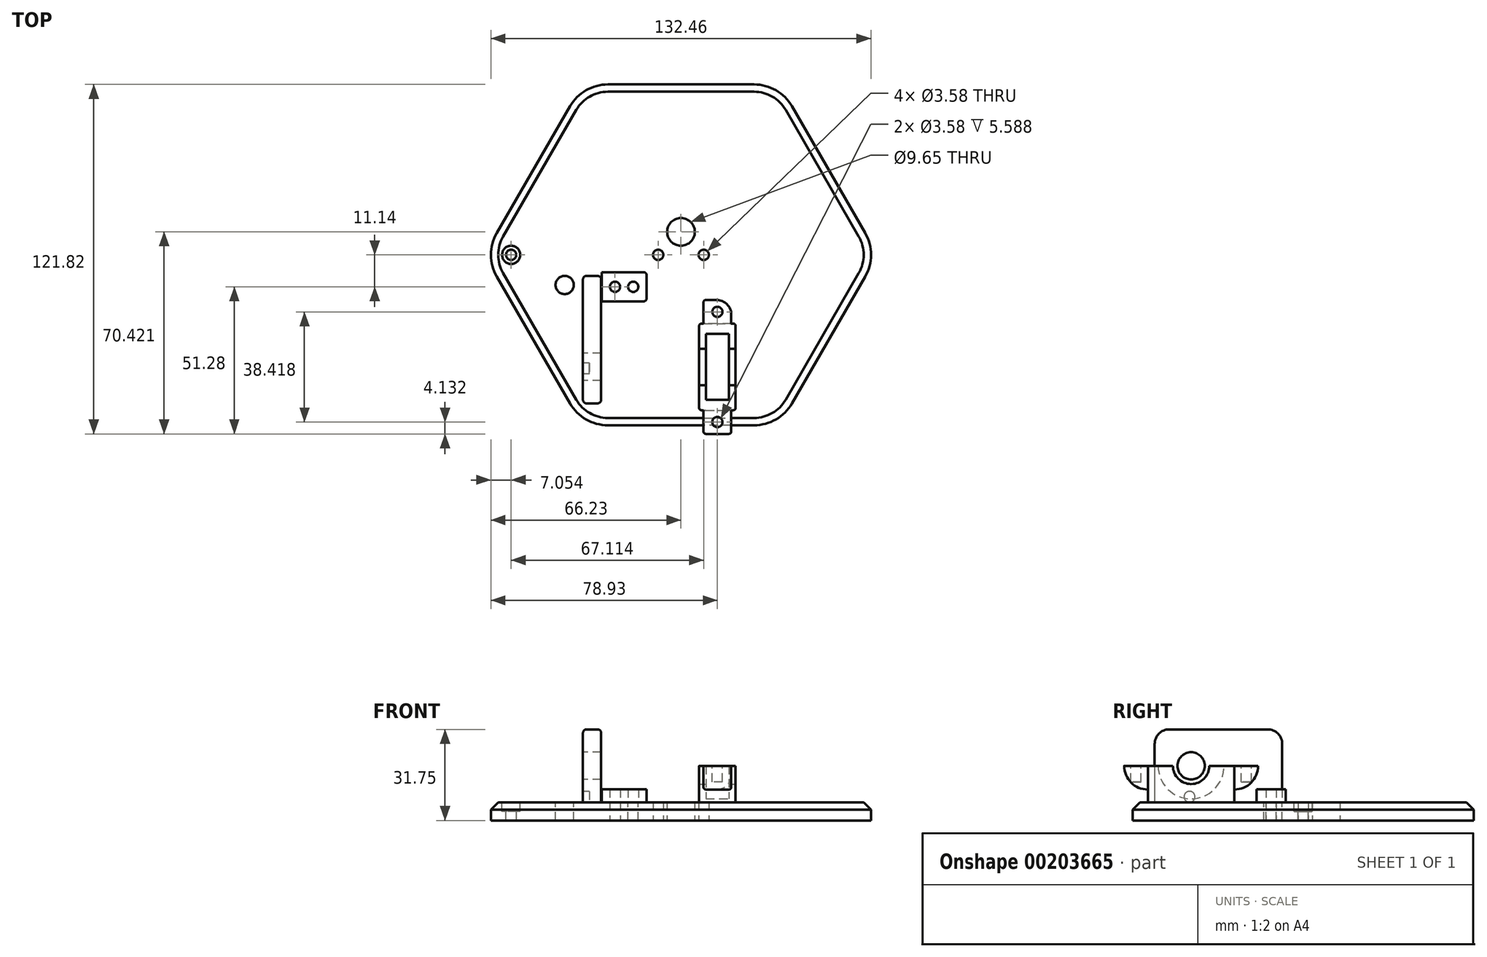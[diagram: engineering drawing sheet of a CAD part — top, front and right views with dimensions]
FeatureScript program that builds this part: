
annotation { "Feature Type Name" : "Feature", "Feature Type Description" : "" }
export const myFeature = defineFeature(function(context is Context, id is Id, definition is map)
    precondition{}
    {
        {
            var Q0;
            Q0=qCreatedBy(makeId("Top.planeOp"),FACE);
            var sketch = newSketch(context, id + "F0", { "sketchPlane" : qUnion([Q0])});
            skCircle(sketch, "E0.cCircle", {"center": v(0, 0) * mm, "radius": 59.4 * mm, "construction": true});
            skLineSegment(sketch, "E0.0", {"start": v(34.3, -59.4) * mm, "end": v(-34.3, -59.4) * mm});
            skLineSegment(sketch, "E0.1", {"start": v(-34.3, -59.4) * mm, "end": v(-68.59, 0) * mm});
            skLineSegment(sketch, "E0.2", {"start": v(-68.59, 0) * mm, "end": v(-34.3, 59.4) * mm});
            skLineSegment(sketch, "E0.3", {"start": v(-34.3, 59.4) * mm, "end": v(34.3, 59.4) * mm});
            skLineSegment(sketch, "E0.4", {"start": v(34.3, 59.4) * mm, "end": v(68.59, 0) * mm});
            skLineSegment(sketch, "E0.5", {"start": v(68.59, 0) * mm, "end": v(34.3, -59.4) * mm});
            skPoint(sketch, "E0.0.midPoint", {"position": v(0, -59.4) * mm});
            skCircle(sketch, "E1", {"center": v(0, 0) * mm, "radius": 3.18 * mm});
            skCircle(sketch, "E2", {"center": v(0, 8) * mm, "radius": 4.83 * mm});
            skCircle(sketch, "E3", {"center": v(0, 0) * mm, "radius": 7.94 * mm, "construction": true});
            skCircle(sketch, "E4", {"center": v(-7.94, 0) * mm, "radius": 1.8 * mm});
            skCircle(sketch, "E5", {"center": v(7.94, 0) * mm, "radius": 1.8 * mm});
            skSolve(sketch);
        }
        {
            var Q0;
            Q0=makeQuery(id+"F0.imprint","IMPRINT",FACE,{"disambiguationData":[TD([[makeQuery(id+"F0.imprint","IMPRINT",EDGE,{"derivedFrom":sQuery(id+"F0.wireOp",EDGE,"E0.0")}),-1.0]])]});
            var Q1;
            Q1=makeQuery(id+"F0.imprint","IMPRINT",FACE,{"disambiguationData":[TD([[makeQuery(id+"F0.imprint","IMPRINT",EDGE,{"derivedFrom":sQuery(id+"F0.wireOp",EDGE,"E1")}),1.0]])]});
            extrude(context, id + "F1", {"entities" : qUnion([Q0, Q1]), "depth" : 6.35 * mm});
        }
        {
            var Q0;
            Q0=makeQuery(id+"F1.opExtrude","CAP_FACE",FACE,{"disambiguationData":[OSD([sQuery(id+"F0.wireOp",EDGE,"E0.0"),sQuery(id+"F0.wireOp",EDGE,"E0.1"),sQuery(id+"F0.wireOp",EDGE,"E0.2"),sQuery(id+"F0.wireOp",EDGE,"E0.3"),sQuery(id+"F0.wireOp",EDGE,"E0.4"),sQuery(id+"F0.wireOp",EDGE,"E0.5"),sQuery(id+"F0.wireOp",EDGE,"E1")])],"isStart":false});
            var sketch = newSketch(context, id + "F2", { "sketchPlane" : qUnion([Q0])});
            skLineSegment(sketch, "E6.bottom", {"start": v(-34.16, -51.78) * mm, "end": v(-27.81, -51.78) * mm});
            skLineSegment(sketch, "E6.top", {"start": v(-34.16, -7.33) * mm, "end": v(-27.81, -7.33) * mm});
            skLineSegment(sketch, "E6.left", {"start": v(-34.16, -51.78) * mm, "end": v(-34.16, -7.33) * mm});
            skLineSegment(sketch, "E6.right", {"start": v(-27.81, -51.78) * mm, "end": v(-27.81, -7.33) * mm});
            skLineSegment(sketch, "E7.bottom", {"start": v(6.35, -54.16) * mm, "end": v(19.05, -54.16) * mm});
            skLineSegment(sketch, "E7.top", {"start": v(6.35, -24) * mm, "end": v(19.05, -24) * mm});
            skLineSegment(sketch, "E7.left", {"start": v(6.35, -54.16) * mm, "end": v(6.35, -24) * mm});
            skLineSegment(sketch, "E7.right", {"start": v(19.05, -54.16) * mm, "end": v(19.05, -24) * mm});
            skLineSegment(sketch, "E8.1.0", {"start": v(37.38, 43.58) * mm, "end": v(11.26, 28.5) * mm});
            skLineSegment(sketch, "E8.1.1", {"start": v(43.73, 32.58) * mm, "end": v(17.6, 17.5) * mm});
            skLineSegment(sketch, "E8.1.2", {"start": v(17.6, 17.5) * mm, "end": v(11.26, 28.5) * mm});
            skLineSegment(sketch, "E8.1.3", {"start": v(61.92, -3.7) * mm, "end": v(23.43, -25.92) * mm});
            skLineSegment(sketch, "E8.1.4", {"start": v(58.75, 1.8) * mm, "end": v(20.25, -20.42) * mm});
            skLineSegment(sketch, "E8.1.5", {"start": v(20.25, -20.42) * mm, "end": v(14.92, -11.18) * mm});
            skLineSegment(sketch, "E8.1.6", {"start": v(26.85, -16.61) * mm, "end": v(21.52, -7.37) * mm});
            skLineSegment(sketch, "E8.1.7", {"start": v(43.73, 32.58) * mm, "end": v(37.38, 43.58) * mm});
            skLineSegment(sketch, "E8.1.8", {"start": v(14.92, -11.18) * mm, "end": v(21.52, -7.37) * mm});
            skLineSegment(sketch, "E8.1.9", {"start": v(61.92, -3.7) * mm, "end": v(58.75, 1.8) * mm});
            skLineSegment(sketch, "E8.1.10", {"start": v(23.43, -25.92) * mm, "end": v(20.25, -20.42) * mm});
            skLineSegment(sketch, "E8.1.11", {"start": v(20.25, -20.42) * mm, "end": v(26.85, -16.61) * mm});
            skLineSegment(sketch, "E8.2.0", {"start": v(-56.43, 10.58) * mm, "end": v(-30.3, -4.5) * mm});
            skLineSegment(sketch, "E8.2.1", {"start": v(-50.08, 21.58) * mm, "end": v(-23.96, 6.5) * mm});
            skLineSegment(sketch, "E8.2.2", {"start": v(-23.96, 6.5) * mm, "end": v(-30.3, -4.5) * mm});
            skLineSegment(sketch, "E8.2.3", {"start": v(-27.76, 55.47) * mm, "end": v(10.74, 33.25) * mm});
            skLineSegment(sketch, "E8.2.4", {"start": v(-30.93, 49.98) * mm, "end": v(7.56, 27.75) * mm});
            skLineSegment(sketch, "E8.2.5", {"start": v(7.56, 27.75) * mm, "end": v(2.23, 18.51) * mm});
            skLineSegment(sketch, "E8.2.6", {"start": v(0.96, 31.56) * mm, "end": v(-4.37, 22.32) * mm});
            skLineSegment(sketch, "E8.2.7", {"start": v(-50.08, 21.58) * mm, "end": v(-56.43, 10.58) * mm});
            skLineSegment(sketch, "E8.2.8", {"start": v(2.23, 18.51) * mm, "end": v(-4.37, 22.32) * mm});
            skLineSegment(sketch, "E8.2.9", {"start": v(-27.76, 55.47) * mm, "end": v(-30.93, 49.98) * mm});
            skLineSegment(sketch, "E8.2.10", {"start": v(10.74, 33.25) * mm, "end": v(7.56, 27.75) * mm});
            skLineSegment(sketch, "E8.2.11", {"start": v(7.56, 27.75) * mm, "end": v(0.96, 31.56) * mm});
            skPoint(sketch, "E8.center", {"position": v(0, 0) * mm});
            skCircle(sketch, "E9", {"center": v(-40.51, -10.5) * mm, "radius": 3.18 * mm});
            skCircle(sketch, "E10", {"center": v(-59.18, 0) * mm, "radius": 1.8 * mm});
            skCircle(sketch, "E11", {"center": v(-59.18, 0) * mm, "radius": 3.18 * mm});
            skCircle(sketch, "E12.1.0", {"center": v(29.59, -51.25) * mm, "radius": 3.18 * mm});
            skCircle(sketch, "E12.1.1", {"center": v(29.59, -51.25) * mm, "radius": 1.8 * mm});
            skCircle(sketch, "E12.2.0", {"center": v(29.59, 51.25) * mm, "radius": 3.18 * mm});
            skCircle(sketch, "E12.2.1", {"center": v(29.59, 51.25) * mm, "radius": 1.8 * mm});
            skCircle(sketch, "E13", {"center": v(-22.97, -11.14) * mm, "radius": 1.8 * mm});
            skPoint(sketch, "E13.centerSnap0", {"position": v(-16.64, -11.14) * mm});
            skCircle(sketch, "E14", {"center": v(-16.62, -11.14) * mm, "radius": 1.8 * mm});
            skCircle(sketch, "E15", {"center": v(0, 0) * mm, "radius": 4.76 * mm});
            skLineSegment(sketch, "E16", {"start": v(-22.97, -11.14) * mm, "end": v(-16.62, -11.14) * mm, "construction": true});
            skLineSegment(sketch, "E17.bottom", {"start": v(-11.98, -6.06) * mm, "end": v(-27.62, -6.06) * mm});
            skLineSegment(sketch, "E17.top", {"start": v(-11.98, -16.22) * mm, "end": v(-27.62, -16.22) * mm});
            skLineSegment(sketch, "E17.left", {"start": v(-11.98, -6.06) * mm, "end": v(-11.98, -16.22) * mm});
            skLineSegment(sketch, "E17.right", {"start": v(-27.62, -6.06) * mm, "end": v(-27.62, -16.22) * mm});
            skPoint(sketch, "E17.middle", {"position": v(-19.8, -11.14) * mm});
            skSolve(sketch);
        }
        {
            var Q0;
            Q0=makeQuery(id+"F2.imprint","IMPRINT",FACE,{"disambiguationData":[TD([[makeQuery(id+"F2.imprint","IMPRINT",EDGE,{"derivedFrom":sQuery(id+"F2.wireOp",EDGE,"E6.bottom")}),1.0]])]});
            extrude(context, id + "F3", {"entities" : qUnion([Q0]), "operationType" : NewBodyOperationType.ADD, "depth" : 25.4 * mm});
        }
        {
            var Q0;
            Q0=makeQuery(id+"F2.imprint","IMPRINT",FACE,{"disambiguationData":[TD([[makeQuery(id+"F2.imprint","IMPRINT",EDGE,{"derivedFrom":sQuery(id+"F2.wireOp",EDGE,"E7.bottom")}),1.0]])]});
            extrude(context, id + "F4", {"entities" : qUnion([Q0]), "operationType" : NewBodyOperationType.ADD, "depth" : 12.7 * mm});
        }
        {
            var Q0;
            Q0=makeQuery(id+"F2.imprint","IMPRINT",FACE,{"disambiguationData":[TD([[makeQuery(id+"F2.imprint","IMPRINT",EDGE,{"derivedFrom":sQuery(id+"F2.wireOp",EDGE,"E9")}),1.0]])]});
            extrude(context, id + "F5", {"entities" : qUnion([Q0]), "operationType" : NewBodyOperationType.REMOVE, "oppositeDirection" : true, "depth" : 25.4 * mm});
        }
        {
            var Q0;
            Q0=sQuery(id+"F2.wireOp",VERTEX,"E10.center");
            var Q1;
            Q1=makeQuery(id+"F1.opExtrude","SWEPT_BODY",BODY,{"disambiguationData":[OSD([sQuery(id+"F0.wireOp",EDGE,"E0.0"),sQuery(id+"F0.wireOp",EDGE,"E0.1"),sQuery(id+"F0.wireOp",EDGE,"E0.2"),sQuery(id+"F0.wireOp",EDGE,"E0.3"),sQuery(id+"F0.wireOp",EDGE,"E0.4"),sQuery(id+"F0.wireOp",EDGE,"E0.5"),sQuery(id+"F0.wireOp",EDGE,"E1")])]});
            hole(context, id + "F6", {"style" : HoleStyle.C_BORE, "endStyle" : HoleEndStyle.BLIND, "holeDiameter" : 3.58 * mm, "cBoreDiameter" : 6.35 * mm, "cBoreDepth" : 3.17 * mm, "holeDepth" : 6.35 * mm, "locations" : qUnion([Q0]), "scope" : qUnion([Q1])});
        }
        {
            var Q0;
            Q0=makeQuery(id+"F2.imprint","IMPRINT",FACE,{"disambiguationData":[TD([[makeQuery(id+"F2.imprint","IMPRINT",EDGE,{"derivedFrom":sQuery(id+"F2.wireOp",EDGE,"E13")}),-1.0]])]});
            extrude(context, id + "F7", {"entities" : qUnion([Q0]), "operationType" : NewBodyOperationType.ADD, "depth" : 4.57 * mm});
        }
        {
            var Q0;
            Q0=makeQuery(id+"F7.opExtrude","SWEPT_EDGE",EDGE,{"disambiguationData":[OSD([sQuery(id+"F2.wireOp",EDGE,"E17.top"),sQuery(id+"F2.wireOp",EDGE,"E17.left")])]});
            var Q1;
            Q1=makeQuery(id+"F7.opExtrude","SWEPT_EDGE",EDGE,{"disambiguationData":[OSD([sQuery(id+"F2.wireOp",EDGE,"E17.bottom"),sQuery(id+"F2.wireOp",EDGE,"E17.left")])]});
            fillet(context, id + "F8", {"entities" : qUnion([Q0, Q1]), "radius" : 1.02 * mm, "tangentPropagation" : true, "allowEdgeOverflow" : false});
        }
        {
            var Q0;
            Q0=makeQuery(id+"F4.opExtrude","CAP_FACE",FACE,{"disambiguationData":[OSD([sQuery(id+"F2.wireOp",EDGE,"E7.bottom"),sQuery(id+"F2.wireOp",EDGE,"E7.top"),sQuery(id+"F2.wireOp",EDGE,"E7.left"),sQuery(id+"F2.wireOp",EDGE,"E7.right")])],"isStart":false});
            var sketch = newSketch(context, id + "F9", { "sketchPlane" : qUnion([Q0])});
            skLineSegment(sketch, "E18.bottom", {"start": v(16.7, -27.58) * mm, "end": v(8.7, -27.58) * mm});
            skLineSegment(sketch, "E18.top", {"start": v(16.7, -50.58) * mm, "end": v(8.7, -50.58) * mm});
            skLineSegment(sketch, "E18.left", {"start": v(16.7, -27.58) * mm, "end": v(16.7, -50.58) * mm});
            skLineSegment(sketch, "E18.right", {"start": v(8.7, -27.58) * mm, "end": v(8.7, -50.58) * mm});
            skPoint(sketch, "E18.middle", {"position": v(12.7, -39.08) * mm});
            skPoint(sketch, "E18.middle.positionSnap0", {"position": v(12.7, -24) * mm});
            skPoint(sketch, "E18.middle.positionSnap1", {"position": v(6.35, -39.08) * mm});
            skPoint(sketch, "E18.centerSnap0", {"position": v(12.7, -24) * mm});
            skPoint(sketch, "E18.centerSnap1", {"position": v(6.35, -39.08) * mm});
            skLineSegment(sketch, "E19", {"start": v(8.7, -39.08) * mm, "end": v(16.7, -39.08) * mm});
            skSolve(sketch);
        }
        {
            var Q0;
            Q0=makeQuery(id+"F9.imprint","IMPRINT",FACE,{"disambiguationData":[TD([[makeQuery(id+"F9.imprint","IMPRINT",EDGE,{"derivedFrom":sQuery(id+"F9.wireOp",EDGE,"E18.bottom")}),1.0]])]});
            var Q1;
            Q1=sQuery(id+"F9.wireOp",EDGE,"E19");
            revolve(context, id + "F10", {"operationType" : NewBodyOperationType.REMOVE, "entities" : qUnion([Q0]), "axis" : qUnion([Q1]), "revolveType" : RevolveType.FULL, "oppositeDirection" : true});
        }
        {
            var Q0;
            Q0=makeQuery(id+"F4.opExtrude","SWEPT_FACE",FACE,{"disambiguationData":[OSD([sQuery(id+"F2.wireOp",EDGE,"E7.top")])]});
            var sketch = newSketch(context, id + "F11", { "sketchPlane" : qUnion([Q0])});
            skLineSegment(sketch, "E20", {"start": v(-12.7, 19.05) * mm, "end": v(-12.7, 10.8) * mm});
            skLineSegment(sketch, "E21.bottom", {"start": v(-17.53, 19.05) * mm, "end": v(-7.87, 19.05) * mm});
            skLineSegment(sketch, "E21.top", {"start": v(-17.53, 10.8) * mm, "end": v(-7.87, 10.8) * mm});
            skLineSegment(sketch, "E21.left", {"start": v(-17.53, 19.05) * mm, "end": v(-17.53, 10.8) * mm});
            skLineSegment(sketch, "E21.right", {"start": v(-7.87, 19.05) * mm, "end": v(-7.87, 10.8) * mm});
            skPoint(sketch, "E21.middle", {"position": v(-12.7, 14.92) * mm});
            skSolve(sketch);
        }
        {
            var Q0;
            Q0=makeQuery(id+"F4.opExtrude","SWEPT_FACE",FACE,{"disambiguationData":[OSD([sQuery(id+"F2.wireOp",EDGE,"E7.bottom")])]});
            var sketch = newSketch(context, id + "F12", { "sketchPlane" : qUnion([Q0])});
            skLineSegment(sketch, "E22", {"start": v(12.7, 19.05) * mm, "end": v(12.7, 10.8) * mm});
            skPoint(sketch, "E22.endSnap0", {"position": v(12.7, 19.05) * mm});
            skLineSegment(sketch, "E23.bottom", {"start": v(7.87, 19.05) * mm, "end": v(17.53, 19.05) * mm});
            skLineSegment(sketch, "E23.top", {"start": v(7.87, 10.8) * mm, "end": v(17.53, 10.8) * mm});
            skLineSegment(sketch, "E23.left", {"start": v(7.87, 19.05) * mm, "end": v(7.87, 10.8) * mm});
            skLineSegment(sketch, "E23.right", {"start": v(17.53, 19.05) * mm, "end": v(17.53, 10.8) * mm});
            skPoint(sketch, "E23.middle", {"position": v(12.7, 14.92) * mm});
            skSolve(sketch);
        }
        {
            var Q0;
            Q0=sQuery(id+"F2.wireOp",VERTEX,"E13.center");
            var Q1;
            Q1=sQuery(id+"F2.wireOp",VERTEX,"E13.centerSnap0");
            var Q2;
            Q2=makeQuery(id+"F1.opExtrude","SWEPT_BODY",BODY,{"disambiguationData":[OSD([sQuery(id+"F0.wireOp",EDGE,"E0.0"),sQuery(id+"F0.wireOp",EDGE,"E0.1"),sQuery(id+"F0.wireOp",EDGE,"E0.2"),sQuery(id+"F0.wireOp",EDGE,"E0.3"),sQuery(id+"F0.wireOp",EDGE,"E0.4"),sQuery(id+"F0.wireOp",EDGE,"E0.5"),sQuery(id+"F0.wireOp",EDGE,"E1")])]});
            hole(context, id + "F13", {"style" : HoleStyle.SIMPLE, "endStyle" : HoleEndStyle.BLIND, "holeDiameter" : 3.58 * mm, "holeDepth" : 6.35 * mm, "locations" : qUnion([Q0, Q1]), "scope" : qUnion([Q2])});
        }
        {
            var Q0;
            {var subQ0=sQuery(id+"F11.wireOp",EDGE,"E20");Q0=makeQuery(id+"F11.imprint","IMPRINT",FACE,{"disambiguationData":[TD([[makeQuery(id+"F11.imprint","IMPRINT",EDGE,{"derivedFrom":subQ0}),-1.0]])]});}
            var Q1;
            {var subQ0=sQuery(id+"F11.wireOp",EDGE,"E20");Q1=makeQuery(id+"F11.imprint","IMPRINT",FACE,{"disambiguationData":[TD([[makeQuery(id+"F11.imprint","IMPRINT",EDGE,{"derivedFrom":subQ0}),1.0]])]});}
            var Q2;
            Q2=sQuery(id+"F11.wireOp",EDGE,"E21.bottom");
            revolve(context, id + "F14", {"operationType" : NewBodyOperationType.ADD, "entities" : qUnion([Q0, Q1]), "axis" : qUnion([Q2]), "revolveType" : RevolveType.ONE_DIRECTION, "oppositeDirection" : true, "angle" : 90 * degree});
        }
        {
            var Q0;
            {var subQ0=sQuery(id+"F12.wireOp",EDGE,"E22");Q0=makeQuery(id+"F12.imprint","IMPRINT",FACE,{"disambiguationData":[TD([[makeQuery(id+"F12.imprint","IMPRINT",EDGE,{"derivedFrom":subQ0}),-1.0]])]});}
            var Q1;
            {var subQ0=sQuery(id+"F12.wireOp",EDGE,"E22");Q1=makeQuery(id+"F12.imprint","IMPRINT",FACE,{"disambiguationData":[TD([[makeQuery(id+"F12.imprint","IMPRINT",EDGE,{"derivedFrom":subQ0}),1.0]])]});}
            var Q2;
            Q2=sQuery(id+"F12.wireOp",EDGE,"E23.bottom");
            revolve(context, id + "F15", {"operationType" : NewBodyOperationType.ADD, "entities" : qUnion([Q0, Q1]), "axis" : qUnion([Q2]), "revolveType" : RevolveType.ONE_DIRECTION, "oppositeDirection" : true, "angle" : 90 * degree});
        }
        {
            var Q0;
            Q0=makeQuery(id+"F4.opExtrude","SWEPT_FACE",FACE,{"disambiguationData":[OSD([sQuery(id+"F2.wireOp",EDGE,"E7.right")])]});
            var sketch = newSketch(context, id + "F16", { "sketchPlane" : qUnion([Q0])});
            skCircle(sketch, "E24", {"center": v(-39.08, 19.05) * mm, "radius": 6.35 * mm});
            skSolve(sketch);
        }
        {
            var Q0;
            {var subQ0=sQuery(id+"F16.wireOp",EDGE,"E24");var subQ1=makeQuery(id+"F4.opExtrude","CAP_EDGE",EDGE,{"disambiguationData":[OSD([sQuery(id+"F2.wireOp",EDGE,"E7.right")])],"isStart":false});var subQ2=makeQuery(id+"F16.imprint","INTERSECT",VERTEX,{"disambiguationData":[OD(0.0)],"derivedFrom":[subQ1,subQ0]});Q0=makeQuery(id+"F16.imprint","IMPRINT",FACE,{"disambiguationData":[TD([[makeQuery(id+"F16.imprint","IMPRINT",EDGE,{"disambiguationData":[TD([[subQ2,1.0]])],"derivedFrom":subQ0}),1.0]])]});}
            var Q1;
            {var subQ0=sQuery(id+"F16.wireOp",EDGE,"E24");var subQ1=makeQuery(id+"F4.opExtrude","CAP_EDGE",EDGE,{"disambiguationData":[OSD([sQuery(id+"F2.wireOp",EDGE,"E7.right")])],"isStart":false});var subQ2=makeQuery(id+"F16.imprint","INTERSECT",VERTEX,{"disambiguationData":[OD(0.0)],"derivedFrom":[subQ1,subQ0]});Q1=makeQuery(id+"F16.imprint","IMPRINT",FACE,{"disambiguationData":[TD([[makeQuery(id+"F16.imprint","IMPRINT",EDGE,{"disambiguationData":[TD([[subQ2,-1.0]])],"derivedFrom":subQ0}),1.0]])]});}
            extrude(context, id + "F17", {"entities" : qUnion([Q0, Q1]), "operationType" : NewBodyOperationType.REMOVE, "oppositeDirection" : true, "depth" : 25.4 * mm});
        }
        {
            var Q0;
            Q0=makeQuery(id+"F3.opExtrude","SWEPT_FACE",FACE,{"disambiguationData":[OSD([sQuery(id+"F2.wireOp",EDGE,"E6.left")])]});
            var sketch = newSketch(context, id + "F18", { "sketchPlane" : qUnion([Q0])});
            skCircle(sketch, "E25", {"center": v(39.08, 19.05) * mm, "radius": 4.76 * mm});
            skSolve(sketch);
        }
        {
            var Q0;
            Q0 = qSketchRegion(id + "F18", true);
            extrude(context, id + "F19", {"entities" : qUnion([Q0]), "operationType" : NewBodyOperationType.REMOVE, "oppositeDirection" : true, "depth" : 19.05 * mm});
        }
        {
            var Q0;
            Q0=makeQuery(id+"F3.opExtrude","SWEPT_FACE",FACE,{"disambiguationData":[OSD([sQuery(id+"F2.wireOp",EDGE,"E6.left")])]});
            var sketch = newSketch(context, id + "F20", { "sketchPlane" : qUnion([Q0])});
            skCircle(sketch, "E26", {"center": v(39.64, 8.26) * mm, "radius": 1.9 * mm});
            skSolve(sketch);
        }
        {
            var Q0;
            {var subQ0=sQuery(id+"F20.wireOp",EDGE,"E26");var subQ1=sQuery(id+"F2.wireOp",EDGE,"E6.left");var subQ2=makeQuery(id+"F26.opFillet","BLEND_EDGE",EDGE,{"blendedFrom":[makeQuery(id+"F3.opExtrude","CAP_EDGE",EDGE,{"disambiguationData":[OSD([subQ1])],"isStart":true}),makeQuery(id+"F3.opExtrude","SWEPT_FACE",FACE,{"disambiguationData":[OSD([subQ1])]})],"blendedInto":[makeQuery(id+"F3.opExtrude","SWEPT_FACE",FACE,{"disambiguationData":[OSD([subQ1])]})]});var subQ3=makeQuery(id+"F20.imprint","INTERSECT",VERTEX,{"disambiguationData":[OD(0.0)],"derivedFrom":[subQ2,subQ0]});Q0=makeQuery(id+"F20.imprint","IMPRINT",FACE,{"disambiguationData":[TD([[makeQuery(id+"F20.imprint","IMPRINT",EDGE,{"disambiguationData":[TD([[subQ3,1.0]])],"derivedFrom":subQ0}),1.0]])]});}
            var Q1;
            {var subQ0=sQuery(id+"F20.wireOp",EDGE,"E26");var subQ1=sQuery(id+"F2.wireOp",EDGE,"E6.left");var subQ2=makeQuery(id+"F26.opFillet","BLEND_EDGE",EDGE,{"blendedFrom":[makeQuery(id+"F3.opExtrude","CAP_EDGE",EDGE,{"disambiguationData":[OSD([subQ1])],"isStart":true}),makeQuery(id+"F3.opExtrude","SWEPT_FACE",FACE,{"disambiguationData":[OSD([subQ1])]})],"blendedInto":[makeQuery(id+"F3.opExtrude","SWEPT_FACE",FACE,{"disambiguationData":[OSD([subQ1])]})]});var subQ3=makeQuery(id+"F20.imprint","INTERSECT",VERTEX,{"disambiguationData":[OD(0.0)],"derivedFrom":[subQ2,subQ0]});Q1=makeQuery(id+"F20.imprint","IMPRINT",FACE,{"disambiguationData":[TD([[makeQuery(id+"F20.imprint","IMPRINT",EDGE,{"disambiguationData":[TD([[subQ3,-1.0]])],"derivedFrom":subQ0}),1.0]])]});}
            extrude(context, id + "F21", {"entities" : qUnion([Q0, Q1]), "operationType" : NewBodyOperationType.REMOVE, "endBound" : BoundingType.SYMMETRIC, "oppositeDirection" : true, "depth" : 4.57 * mm});
        }
        {
            var Q0;
            {var subQ0=sQuery(id+"F11.wireOp",EDGE,"E21.right");var subQ1=sQuery(id+"F2.wireOp",EDGE,"E7.right");var subQ2=sQuery(id+"F2.wireOp",EDGE,"E7.left");var subQ3=sQuery(id+"F2.wireOp",EDGE,"E7.top");var subQ4=sQuery(id+"F11.wireOp",EDGE,"E21.top");var subQ5=sQuery(id+"F11.wireOp",EDGE,"E21.left");var subQ6=sQuery(id+"F2.wireOp",EDGE,"E7.bottom");Q0=makeQuery(id+"F17.boolean.opBoolean","SPLIT",FACE,{"disambiguationData":[TD([makeQuery(id+"F4.opExtrude","SWEPT_FACE",FACE,{"disambiguationData":[OSD([subQ3])]})])],"derivedFrom":makeQuery(id+"FIzczD0P8AIGJL4_1.boolean.opBoolean","MERGE",FACE,{"derivedFrom":[makeQuery(id+"F14.boolean.opBoolean","MERGE",FACE,{"derivedFrom":[makeQuery(id+"F4.opExtrude","CAP_FACE",FACE,{"disambiguationData":[OSD([subQ6,subQ3,subQ2,subQ1])],"isStart":false}),makeQuery(id+"F14.opRevolve","CAP_FACE",FACE,{"disambiguationData":[OSD([sQuery(id+"F11.wireOp",EDGE,"E21.bottom"),subQ4,subQ5,subQ0])],"isStart":false})]}),makeQuery(id+"FIzczD0P8AIGJL4_1.opRevolve","CAP_FACE",FACE,{"disambiguationData":[OSD([subQ6,sQuery(id+"F12.wireOp",EDGE,"E23.top"),sQuery(id+"F12.wireOp",EDGE,"E23.left"),sQuery(id+"F12.wireOp",EDGE,"E23.right")])],"isStart":false})]})});}
            var sketch = newSketch(context, id + "F22", { "sketchPlane" : qUnion([Q0])});
            skCircle(sketch, "E27", {"center": v(12.7, -19.87) * mm, "radius": 1.8 * mm});
            skPoint(sketch, "E27.centerSnap0", {"position": v(12.7, -15.74) * mm});
            skPoint(sketch, "E27.centerSnap1", {"position": v(7.87, -19.87) * mm});
            skSolve(sketch);
        }
        {
            var Q0;
            {var subQ0=sQuery(id+"F2.wireOp",EDGE,"E7.right");var subQ1=sQuery(id+"F12.wireOp",EDGE,"E23.left");var subQ2=sQuery(id+"F12.wireOp",EDGE,"E23.right");var subQ3=sQuery(id+"F2.wireOp",EDGE,"E7.left");var subQ4=sQuery(id+"F2.wireOp",EDGE,"E7.bottom");var subQ5=sQuery(id+"F12.wireOp",EDGE,"E23.top");Q0=makeQuery(id+"F17.boolean.opBoolean","SPLIT",FACE,{"disambiguationData":[TD([makeQuery(id+"F4.opExtrude","SWEPT_FACE",FACE,{"disambiguationData":[OSD([subQ4])]})])],"derivedFrom":makeQuery(id+"FIzczD0P8AIGJL4_1.boolean.opBoolean","MERGE",FACE,{"derivedFrom":[makeQuery(id+"F14.boolean.opBoolean","MERGE",FACE,{"derivedFrom":[makeQuery(id+"F4.opExtrude","CAP_FACE",FACE,{"disambiguationData":[OSD([subQ4,sQuery(id+"F2.wireOp",EDGE,"E7.top"),subQ3,subQ0])],"isStart":false}),makeQuery(id+"F14.opRevolve","CAP_FACE",FACE,{"disambiguationData":[OSD([sQuery(id+"F11.wireOp",EDGE,"E21.bottom"),sQuery(id+"F11.wireOp",EDGE,"E21.top"),sQuery(id+"F11.wireOp",EDGE,"E21.left"),sQuery(id+"F11.wireOp",EDGE,"E21.right")])],"isStart":false})]}),makeQuery(id+"FIzczD0P8AIGJL4_1.opRevolve","CAP_FACE",FACE,{"disambiguationData":[OSD([subQ4,subQ5,subQ1,subQ2])],"isStart":false})]})});}
            var sketch = newSketch(context, id + "F23", { "sketchPlane" : qUnion([Q0])});
            skCircle(sketch, "E28", {"center": v(12.7, -58.29) * mm, "radius": 1.8 * mm});
            skPoint(sketch, "E28.centerSnap0", {"position": v(12.7, -62.42) * mm});
            skPoint(sketch, "E28.centerSnap1", {"position": v(9.53, -58.29) * mm});
            skSolve(sketch);
        }
        {
            var Q0;
            Q0=makeQuery(id+"F22.imprint","IMPRINT",FACE,{"disambiguationData":[TD([[makeQuery(id+"F22.imprint","IMPRINT",EDGE,{"derivedFrom":sQuery(id+"F22.wireOp",EDGE,"E27")}),1.0]])]});
            var Q1;
            Q1=makeQuery(id+"F23.imprint","IMPRINT",FACE,{"disambiguationData":[TD([[makeQuery(id+"F23.imprint","IMPRINT",EDGE,{"derivedFrom":sQuery(id+"F23.wireOp",EDGE,"E28")}),1.0]])]});
            extrude(context, id + "F24", {"entities" : qUnion([Q0, Q1]), "operationType" : NewBodyOperationType.REMOVE, "oppositeDirection" : true, "depth" : 5.6 * mm});
        }
        {
            var Q0;
            Q0=makeQuery(id+"F3.opExtrude","CAP_EDGE",EDGE,{"disambiguationData":[OSD([sQuery(id+"F2.wireOp",EDGE,"E6.top")])],"isStart":false});
            var Q1;
            Q1=makeQuery(id+"F3.opExtrude","CAP_EDGE",EDGE,{"disambiguationData":[OSD([sQuery(id+"F2.wireOp",EDGE,"E6.bottom")])],"isStart":false});
            fillet(context, id + "F25", {"entities" : qUnion([Q0, Q1]), "radius" : 5.08 * mm, "tangentPropagation" : true, "allowEdgeOverflow" : false});
        }
        {
            var Q0;
            Q0=makeQuery(id+"F3.opExtrude","CAP_EDGE",EDGE,{"disambiguationData":[OSD([sQuery(id+"F2.wireOp",EDGE,"E6.right")])],"isStart":false});
            var Q1;
            Q1=makeQuery(id+"F25.opFillet","BLEND_EDGE",EDGE,{"blendedFrom":[makeQuery(id+"F3.opExtrude","CAP_EDGE",EDGE,{"disambiguationData":[OSD([sQuery(id+"F2.wireOp",EDGE,"E6.bottom")])],"isStart":false}),makeQuery(id+"F3.opExtrude","SWEPT_FACE",FACE,{"disambiguationData":[OSD([sQuery(id+"F2.wireOp",EDGE,"E6.right")])]})],"blendedInto":[makeQuery(id+"F3.opExtrude","SWEPT_FACE",FACE,{"disambiguationData":[OSD([sQuery(id+"F2.wireOp",EDGE,"E6.right")])]})]});
            var Q2;
            Q2=makeQuery(id+"F3.opExtrude","SWEPT_EDGE",EDGE,{"disambiguationData":[OSD([sQuery(id+"F2.wireOp",EDGE,"E6.bottom"),sQuery(id+"F2.wireOp",EDGE,"E6.right")])]});
            var Q3;
            Q3=makeQuery(id+"F3.opExtrude","CAP_EDGE",EDGE,{"disambiguationData":[OSD([sQuery(id+"F2.wireOp",EDGE,"E6.left")])],"isStart":false});
            var Q4;
            Q4=makeQuery(id+"F25.opFillet","BLEND_EDGE",EDGE,{"blendedFrom":[makeQuery(id+"F3.opExtrude","CAP_EDGE",EDGE,{"disambiguationData":[OSD([sQuery(id+"F2.wireOp",EDGE,"E6.bottom")])],"isStart":false}),makeQuery(id+"F3.opExtrude","SWEPT_FACE",FACE,{"disambiguationData":[OSD([sQuery(id+"F2.wireOp",EDGE,"E6.left")])]})],"blendedInto":[makeQuery(id+"F3.opExtrude","SWEPT_FACE",FACE,{"disambiguationData":[OSD([sQuery(id+"F2.wireOp",EDGE,"E6.left")])]})]});
            var Q5;
            Q5=makeQuery(id+"F3.opExtrude","SWEPT_EDGE",EDGE,{"disambiguationData":[OSD([sQuery(id+"F2.wireOp",EDGE,"E6.bottom"),sQuery(id+"F2.wireOp",EDGE,"E6.left")])]});
            var Q6;
            Q6=makeQuery(id+"F25.opFillet","BLEND_EDGE",EDGE,{"blendedFrom":[makeQuery(id+"F3.opExtrude","CAP_EDGE",EDGE,{"disambiguationData":[OSD([sQuery(id+"F2.wireOp",EDGE,"E6.top")])],"isStart":false}),makeQuery(id+"F3.opExtrude","SWEPT_FACE",FACE,{"disambiguationData":[OSD([sQuery(id+"F2.wireOp",EDGE,"E6.right")])]})],"blendedInto":[makeQuery(id+"F3.opExtrude","SWEPT_FACE",FACE,{"disambiguationData":[OSD([sQuery(id+"F2.wireOp",EDGE,"E6.right")])]})]});
            var Q7;
            Q7=makeQuery(id+"F25.opFillet","BLEND_EDGE",EDGE,{"blendedFrom":[makeQuery(id+"F3.opExtrude","CAP_EDGE",EDGE,{"disambiguationData":[OSD([sQuery(id+"F2.wireOp",EDGE,"E6.top")])],"isStart":false}),makeQuery(id+"F3.opExtrude","SWEPT_FACE",FACE,{"disambiguationData":[OSD([sQuery(id+"F2.wireOp",EDGE,"E6.left")])]})],"blendedInto":[makeQuery(id+"F3.opExtrude","SWEPT_FACE",FACE,{"disambiguationData":[OSD([sQuery(id+"F2.wireOp",EDGE,"E6.left")])]})]});
            var Q8;
            Q8=makeQuery(id+"F3.opExtrude","SWEPT_EDGE",EDGE,{"disambiguationData":[OSD([sQuery(id+"F2.wireOp",EDGE,"E6.top"),sQuery(id+"F2.wireOp",EDGE,"E6.right")])]});
            var Q9;
            Q9=makeQuery(id+"F3.opExtrude","SWEPT_EDGE",EDGE,{"disambiguationData":[OSD([sQuery(id+"F2.wireOp",EDGE,"E6.top"),sQuery(id+"F2.wireOp",EDGE,"E6.left")])]});
            fillet(context, id + "F26", {"entities" : qUnion([Q0, Q1, Q2, Q3, Q4, Q5, Q6, Q7, Q8, Q9]), "radius" : 1.27 * mm, "allowEdgeOverflow" : false});
        }
        {
            var Q0;
            Q0=makeQuery(id+"F14.opRevolve","SWEPT_EDGE",EDGE,{"disambiguationData":[OSD([sQuery(id+"F11.wireOp",EDGE,"E21.top"),sQuery(id+"F11.wireOp",EDGE,"E21.left")])]});
            fillet(context, id + "F27", {"entities" : qUnion([Q0]), "radius" : 5.08 * mm, "tangentPropagation" : true, "allowEdgeOverflow" : false});
        }
        {
            var Q0;
            Q0=makeQuery(id+"F4.opExtrude","SWEPT_EDGE",EDGE,{"disambiguationData":[OSD([sQuery(id+"F2.wireOp",EDGE,"E7.bottom"),sQuery(id+"F2.wireOp",EDGE,"E7.left")])]});
            var Q1;
            Q1=makeQuery(id+"F4.opExtrude","SWEPT_EDGE",EDGE,{"disambiguationData":[OSD([sQuery(id+"F2.wireOp",EDGE,"E7.bottom"),sQuery(id+"F2.wireOp",EDGE,"E7.right")])]});
            var Q2;
            Q2=makeQuery(id+"F4.opExtrude","CAP_EDGE",EDGE,{"disambiguationData":[OSD([sQuery(id+"F2.wireOp",EDGE,"E7.right")])],"isStart":true});
            var Q3;
            Q3=makeQuery(id+"F4.opExtrude","SWEPT_EDGE",EDGE,{"disambiguationData":[OSD([sQuery(id+"F2.wireOp",EDGE,"E7.top"),sQuery(id+"F2.wireOp",EDGE,"E7.right")])]});
            var Q4;
            Q4=makeQuery(id+"F4.opExtrude","SWEPT_EDGE",EDGE,{"disambiguationData":[OSD([sQuery(id+"F2.wireOp",EDGE,"E7.top"),sQuery(id+"F2.wireOp",EDGE,"E7.left")])]});
            var Q5;
            Q5=makeQuery(id+"F14.opRevolve","SWEPT_EDGE",EDGE,{"disambiguationData":[OSD([sQuery(id+"F11.wireOp",EDGE,"E21.top"),sQuery(id+"F11.wireOp",EDGE,"E21.right")])]});
            var Q6;
            Q6=makeQuery(id+"F14.opRevolve","CAP_EDGE",EDGE,{"disambiguationData":[OSD([sQuery(id+"F11.wireOp",EDGE,"E21.right")])],"isStart":true});
            var Q7;
            Q7=makeQuery(id+"F14.opRevolve","CAP_EDGE",EDGE,{"disambiguationData":[OSD([sQuery(id+"F11.wireOp",EDGE,"E21.left")])],"isStart":true});
            var Q8;
            Q8=makeQuery(id+"F15.opRevolve","SWEPT_EDGE",EDGE,{"disambiguationData":[OSD([sQuery(id+"F12.wireOp",EDGE,"E23.top"),sQuery(id+"F12.wireOp",EDGE,"E23.left")])]});
            var Q9;
            Q9=makeQuery(id+"F15.opRevolve","SWEPT_EDGE",EDGE,{"disambiguationData":[OSD([sQuery(id+"F12.wireOp",EDGE,"E23.top"),sQuery(id+"F12.wireOp",EDGE,"E23.right")])]});
            fillet(context, id + "F28", {"entities" : qUnion([Q0, Q1, Q2, Q3, Q4, Q5, Q6, Q7, Q8, Q9]), "radius" : 0.76 * mm, "tangentPropagation" : true, "allowEdgeOverflow" : false});
        }
        {
            var Q0;
            Q0=makeQuery(id+"F1.opExtrude","SWEPT_EDGE",EDGE,{"disambiguationData":[OSD([sQuery(id+"F0.wireOp",EDGE,"E0.2"),sQuery(id+"F0.wireOp",EDGE,"E0.3")])]});
            var Q1;
            Q1=makeQuery(id+"F1.opExtrude","SWEPT_EDGE",EDGE,{"disambiguationData":[OSD([sQuery(id+"F0.wireOp",EDGE,"E0.1"),sQuery(id+"F0.wireOp",EDGE,"E0.2")])]});
            var Q2;
            Q2=makeQuery(id+"F1.opExtrude","SWEPT_EDGE",EDGE,{"disambiguationData":[OSD([sQuery(id+"F0.wireOp",EDGE,"E0.3"),sQuery(id+"F0.wireOp",EDGE,"E0.4")])]});
            var Q3;
            Q3=makeQuery(id+"F1.opExtrude","SWEPT_EDGE",EDGE,{"disambiguationData":[OSD([sQuery(id+"F0.wireOp",EDGE,"E0.0"),sQuery(id+"F0.wireOp",EDGE,"E0.1")])]});
            var Q4;
            Q4=makeQuery(id+"F1.opExtrude","SWEPT_EDGE",EDGE,{"disambiguationData":[OSD([sQuery(id+"F0.wireOp",EDGE,"E0.0"),sQuery(id+"F0.wireOp",EDGE,"E0.5")])]});
            var Q5;
            Q5=makeQuery(id+"F1.opExtrude","SWEPT_EDGE",EDGE,{"disambiguationData":[OSD([sQuery(id+"F0.wireOp",EDGE,"E0.4"),sQuery(id+"F0.wireOp",EDGE,"E0.5")])]});
            fillet(context, id + "F29", {"entities" : qUnion([Q0, Q1, Q2, Q3, Q4, Q5]), "radius" : 15.24 * mm, "tangentPropagation" : true, "allowEdgeOverflow" : false});
        }
        {
            var Q0;
            Q0=makeQuery(id+"F1.opExtrude","CAP_EDGE",EDGE,{"disambiguationData":[OSD([sQuery(id+"F0.wireOp",EDGE,"E0.2")])],"isStart":false});
            var Q1;
            Q1=makeQuery(id+"F1.opExtrude","CAP_EDGE",EDGE,{"disambiguationData":[OSD([sQuery(id+"F0.wireOp",EDGE,"E0.1")])],"isStart":false});
            var Q2;
            {var subQ0=sQuery(id+"F0.wireOp",EDGE,"E0.2");var subQ1=sQuery(id+"F0.wireOp",EDGE,"E0.1");Q2=makeQuery(id+"F29.opFillet","BLEND_EDGE",EDGE,{"blendedFrom":[makeQuery(id+"F1.opExtrude","SWEPT_EDGE",EDGE,{"disambiguationData":[OSD([subQ1,subQ0])]}),makeQuery(id+"F1.opExtrude","CAP_FACE",FACE,{"disambiguationData":[OSD([sQuery(id+"F0.wireOp",EDGE,"E0.0"),subQ1,subQ0,sQuery(id+"F0.wireOp",EDGE,"E0.3"),sQuery(id+"F0.wireOp",EDGE,"E0.4"),sQuery(id+"F0.wireOp",EDGE,"E0.5"),sQuery(id+"F0.wireOp",EDGE,"E1")])],"isStart":false})],"blendedInto":[makeQuery(id+"F1.opExtrude","CAP_FACE",FACE,{"disambiguationData":[OSD([sQuery(id+"F0.wireOp",EDGE,"E0.0"),subQ1,subQ0,sQuery(id+"F0.wireOp",EDGE,"E0.3"),sQuery(id+"F0.wireOp",EDGE,"E0.4"),sQuery(id+"F0.wireOp",EDGE,"E0.5"),sQuery(id+"F0.wireOp",EDGE,"E1")])],"isStart":false})]});}
            var Q3;
            {var subQ0=sQuery(id+"F0.wireOp",EDGE,"E0.1");var subQ1=sQuery(id+"F0.wireOp",EDGE,"E0.0");Q3=makeQuery(id+"F29.opFillet","BLEND_EDGE",EDGE,{"blendedFrom":[makeQuery(id+"F1.opExtrude","SWEPT_EDGE",EDGE,{"disambiguationData":[OSD([subQ1,subQ0])]}),makeQuery(id+"F1.opExtrude","CAP_FACE",FACE,{"disambiguationData":[OSD([subQ1,subQ0,sQuery(id+"F0.wireOp",EDGE,"E0.2"),sQuery(id+"F0.wireOp",EDGE,"E0.3"),sQuery(id+"F0.wireOp",EDGE,"E0.4"),sQuery(id+"F0.wireOp",EDGE,"E0.5"),sQuery(id+"F0.wireOp",EDGE,"E1")])],"isStart":false})],"blendedInto":[makeQuery(id+"F1.opExtrude","CAP_FACE",FACE,{"disambiguationData":[OSD([subQ1,subQ0,sQuery(id+"F0.wireOp",EDGE,"E0.2"),sQuery(id+"F0.wireOp",EDGE,"E0.3"),sQuery(id+"F0.wireOp",EDGE,"E0.4"),sQuery(id+"F0.wireOp",EDGE,"E0.5"),sQuery(id+"F0.wireOp",EDGE,"E1")])],"isStart":false})]});}
            var Q4;
            Q4=makeQuery(id+"F1.opExtrude","CAP_EDGE",EDGE,{"disambiguationData":[OSD([sQuery(id+"F0.wireOp",EDGE,"E0.0")])],"isStart":false});
            var Q5;
            {var subQ0=sQuery(id+"F0.wireOp",EDGE,"E0.5");var subQ1=sQuery(id+"F0.wireOp",EDGE,"E0.0");Q5=makeQuery(id+"F29.opFillet","BLEND_EDGE",EDGE,{"blendedFrom":[makeQuery(id+"F1.opExtrude","SWEPT_EDGE",EDGE,{"disambiguationData":[OSD([subQ1,subQ0])]}),makeQuery(id+"F1.opExtrude","CAP_FACE",FACE,{"disambiguationData":[OSD([subQ1,sQuery(id+"F0.wireOp",EDGE,"E0.1"),sQuery(id+"F0.wireOp",EDGE,"E0.2"),sQuery(id+"F0.wireOp",EDGE,"E0.3"),sQuery(id+"F0.wireOp",EDGE,"E0.4"),subQ0,sQuery(id+"F0.wireOp",EDGE,"E1")])],"isStart":false})],"blendedInto":[makeQuery(id+"F1.opExtrude","CAP_FACE",FACE,{"disambiguationData":[OSD([subQ1,sQuery(id+"F0.wireOp",EDGE,"E0.1"),sQuery(id+"F0.wireOp",EDGE,"E0.2"),sQuery(id+"F0.wireOp",EDGE,"E0.3"),sQuery(id+"F0.wireOp",EDGE,"E0.4"),subQ0,sQuery(id+"F0.wireOp",EDGE,"E1")])],"isStart":false})]});}
            var Q6;
            Q6=makeQuery(id+"F1.opExtrude","CAP_EDGE",EDGE,{"disambiguationData":[OSD([sQuery(id+"F0.wireOp",EDGE,"E0.5")])],"isStart":false});
            var Q7;
            {var subQ0=sQuery(id+"F0.wireOp",EDGE,"E0.5");var subQ1=sQuery(id+"F0.wireOp",EDGE,"E0.4");Q7=makeQuery(id+"F29.opFillet","BLEND_EDGE",EDGE,{"blendedFrom":[makeQuery(id+"F1.opExtrude","SWEPT_EDGE",EDGE,{"disambiguationData":[OSD([subQ1,subQ0])]}),makeQuery(id+"F1.opExtrude","CAP_FACE",FACE,{"disambiguationData":[OSD([sQuery(id+"F0.wireOp",EDGE,"E0.0"),sQuery(id+"F0.wireOp",EDGE,"E0.1"),sQuery(id+"F0.wireOp",EDGE,"E0.2"),sQuery(id+"F0.wireOp",EDGE,"E0.3"),subQ1,subQ0,sQuery(id+"F0.wireOp",EDGE,"E1")])],"isStart":false})],"blendedInto":[makeQuery(id+"F1.opExtrude","CAP_FACE",FACE,{"disambiguationData":[OSD([sQuery(id+"F0.wireOp",EDGE,"E0.0"),sQuery(id+"F0.wireOp",EDGE,"E0.1"),sQuery(id+"F0.wireOp",EDGE,"E0.2"),sQuery(id+"F0.wireOp",EDGE,"E0.3"),subQ1,subQ0,sQuery(id+"F0.wireOp",EDGE,"E1")])],"isStart":false})]});}
            var Q8;
            Q8=makeQuery(id+"F1.opExtrude","CAP_EDGE",EDGE,{"disambiguationData":[OSD([sQuery(id+"F0.wireOp",EDGE,"E0.4")])],"isStart":false});
            var Q9;
            {var subQ0=sQuery(id+"F0.wireOp",EDGE,"E0.4");var subQ1=sQuery(id+"F0.wireOp",EDGE,"E0.3");Q9=makeQuery(id+"F29.opFillet","BLEND_EDGE",EDGE,{"blendedFrom":[makeQuery(id+"F1.opExtrude","SWEPT_EDGE",EDGE,{"disambiguationData":[OSD([subQ1,subQ0])]}),makeQuery(id+"F1.opExtrude","CAP_FACE",FACE,{"disambiguationData":[OSD([sQuery(id+"F0.wireOp",EDGE,"E0.0"),sQuery(id+"F0.wireOp",EDGE,"E0.1"),sQuery(id+"F0.wireOp",EDGE,"E0.2"),subQ1,subQ0,sQuery(id+"F0.wireOp",EDGE,"E0.5"),sQuery(id+"F0.wireOp",EDGE,"E1")])],"isStart":false})],"blendedInto":[makeQuery(id+"F1.opExtrude","CAP_FACE",FACE,{"disambiguationData":[OSD([sQuery(id+"F0.wireOp",EDGE,"E0.0"),sQuery(id+"F0.wireOp",EDGE,"E0.1"),sQuery(id+"F0.wireOp",EDGE,"E0.2"),subQ1,subQ0,sQuery(id+"F0.wireOp",EDGE,"E0.5"),sQuery(id+"F0.wireOp",EDGE,"E1")])],"isStart":false})]});}
            var Q10;
            Q10=makeQuery(id+"F1.opExtrude","CAP_EDGE",EDGE,{"disambiguationData":[OSD([sQuery(id+"F0.wireOp",EDGE,"E0.3")])],"isStart":false});
            var Q11;
            {var subQ0=sQuery(id+"F0.wireOp",EDGE,"E0.3");var subQ1=sQuery(id+"F0.wireOp",EDGE,"E0.2");Q11=makeQuery(id+"F29.opFillet","BLEND_EDGE",EDGE,{"blendedFrom":[makeQuery(id+"F1.opExtrude","SWEPT_EDGE",EDGE,{"disambiguationData":[OSD([subQ1,subQ0])]}),makeQuery(id+"F1.opExtrude","CAP_FACE",FACE,{"disambiguationData":[OSD([sQuery(id+"F0.wireOp",EDGE,"E0.0"),sQuery(id+"F0.wireOp",EDGE,"E0.1"),subQ1,subQ0,sQuery(id+"F0.wireOp",EDGE,"E0.4"),sQuery(id+"F0.wireOp",EDGE,"E0.5"),sQuery(id+"F0.wireOp",EDGE,"E1")])],"isStart":false})],"blendedInto":[makeQuery(id+"F1.opExtrude","CAP_FACE",FACE,{"disambiguationData":[OSD([sQuery(id+"F0.wireOp",EDGE,"E0.0"),sQuery(id+"F0.wireOp",EDGE,"E0.1"),subQ1,subQ0,sQuery(id+"F0.wireOp",EDGE,"E0.4"),sQuery(id+"F0.wireOp",EDGE,"E0.5"),sQuery(id+"F0.wireOp",EDGE,"E1")])],"isStart":false})]});}
            chamfer(context, id + "F30", {"entities" : qUnion([Q0, Q1, Q2, Q3, Q4, Q5, Q6, Q7, Q8, Q9, Q10, Q11]), "width" : 2.54 * mm, "tangentPropagation" : true});
        }
        {
            var Q0;
            Q0=makeQuery(id+"F3.opExtrude","SWEPT_FACE",FACE,{"disambiguationData":[OSD([sQuery(id+"F2.wireOp",EDGE,"E6.bottom")])]});
            cPlane(context, id + "F31", {"entities" : qUnion([Q0]), "cplaneType" : CPlaneType.OFFSET, "offset" : 2.54 * mm, "width" : 152.4 * mm, "height" : 152.4 * mm});
        }
        {
            var Q0;
            Q0=qCreatedBy(id+"F31.planeOp",FACE);
            var sketch = newSketch(context, id + "F32", { "sketchPlane" : qUnion([Q0])});
            skCircle(sketch, "E29", {"center": v(-24.66, 7.94) * mm, "radius": 1.54 * mm});
            skSolve(sketch);
        }
        {
            var Q0;
            Q0=makeQuery(id+"F2.imprint","IMPRINT",FACE,{"disambiguationData":[TD([[makeQuery(id+"F2.imprint","IMPRINT",EDGE,{"derivedFrom":makeQuery(id+"F1.opExtrude","CAP_EDGE",EDGE,{"disambiguationData":[OSD([sQuery(id+"F0.wireOp",EDGE,"E2")])],"isStart":false})}),1.0]])]});
            extrude(context, id + "F33", {"entities" : qUnion([Q0]), "operationType" : NewBodyOperationType.REMOVE, "depth" : 11.8 * mm});
        }
    });
